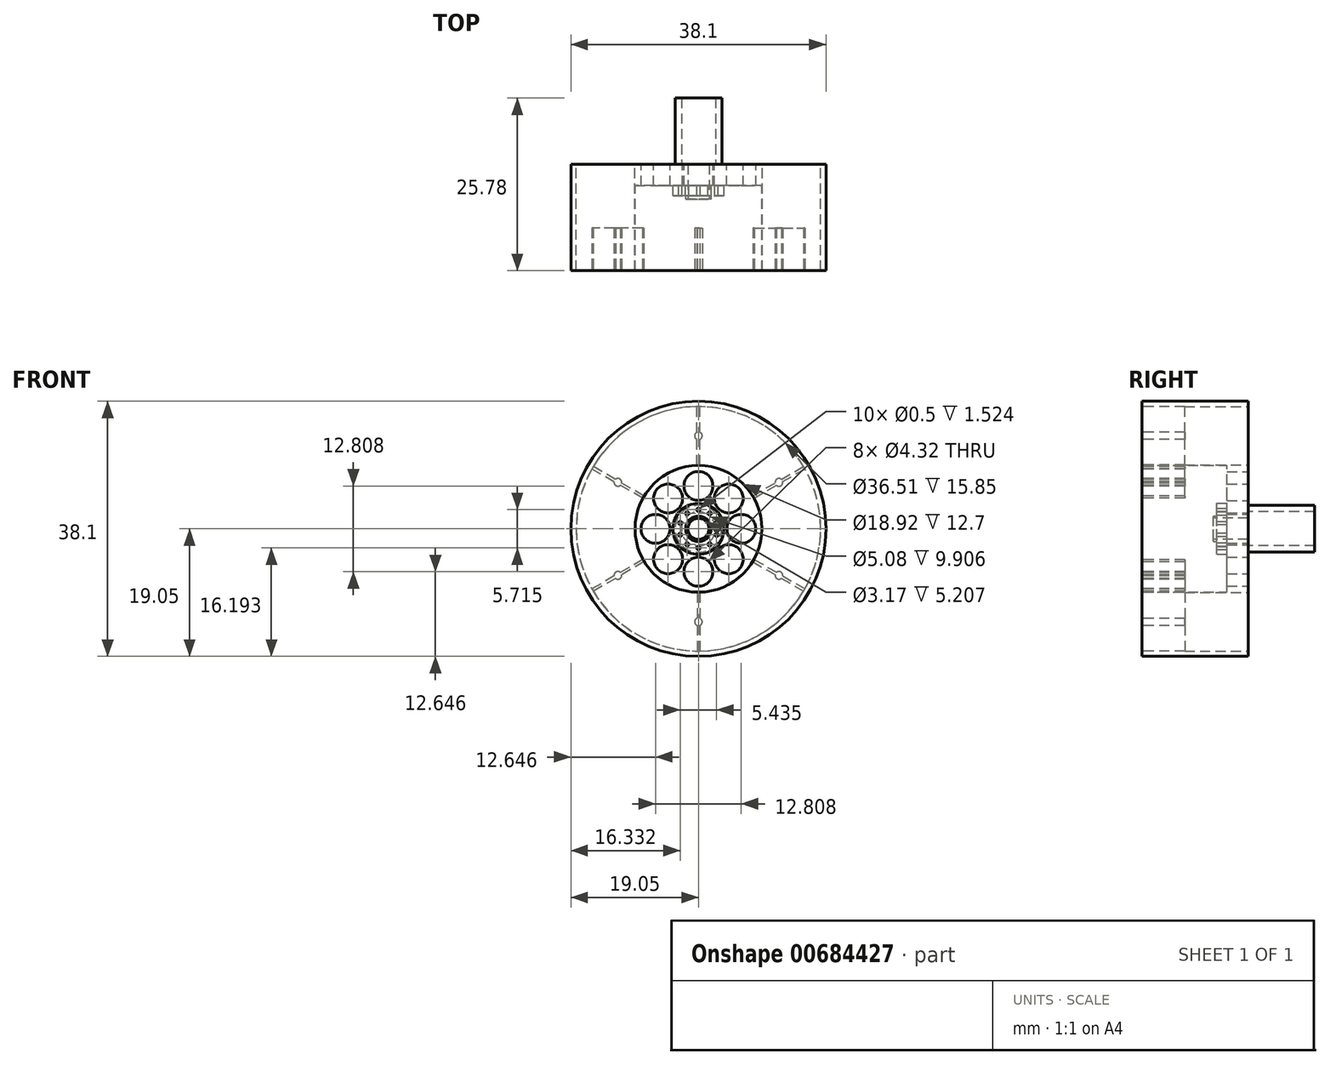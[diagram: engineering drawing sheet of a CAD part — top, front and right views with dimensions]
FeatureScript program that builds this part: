
annotation { "Feature Type Name" : "Feature", "Feature Type Description" : "" }
export const myFeature = defineFeature(function(context is Context, id is Id, definition is map)
    precondition{}
    {
        {
            var Q0;
            Q0=qCreatedBy(makeId("Front.planeOp"),FACE);
            var sketch = newSketch(context, id + "F0", { "sketchPlane" : qUnion([Q0])});
            skCircle(sketch, "E0", {"center": v(0, 0) * mm, "radius": 19.05 * mm});
            skCircle(sketch, "E1", {"center": v(0, 0) * mm, "radius": 17.46 * mm});
            skSolve(sketch);
        }
        {
            var Q0;
            Q0 = qSketchRegion(id + "F0", true);
            extrude(context, id + "F1", {"entities" : qUnion([Q0]), "oppositeDirection" : true, "depth" : 15.88 * mm, "offsetDistance" : 25.4 * mm});
        }
        {
            var Q0;
            Q0=makeQuery(id+"F0.imprint","IMPRINT",FACE,{"disambiguationData":[TD([[makeQuery(id+"F0.imprint","IMPRINT",EDGE,{"derivedFrom":sQuery(id+"F0.wireOp",EDGE,"E1")}),1.0]])]});
            extrude(context, id + "F2", {"entities" : qUnion([Q0]), "operationType" : NewBodyOperationType.ADD, "oppositeDirection" : true, "depth" : 15.88 * mm, "offsetDistance" : 25.4 * mm});
        }
        {
            var Q0;
            {var subQ0=sQuery(id+"F0.wireOp",EDGE,"E1");Q0=makeQuery(id+"F2.boolean.opBoolean","MERGE",FACE,{"derivedFrom":[makeQuery(id+"F1.opExtrude","CAP_FACE",FACE,{"disambiguationData":[OSD([sQuery(id+"F0.wireOp",EDGE,"E0"),subQ0])],"isStart":true}),makeQuery(id+"F2.opExtrude","CAP_FACE",FACE,{"disambiguationData":[OSD([subQ0])],"isStart":true})]});}
            var sketch = newSketch(context, id + "F3", { "sketchPlane" : qUnion([Q0])});
            skCircle(sketch, "E2", {"center": v(0, 0) * mm, "radius": 9.53 * mm});
            skSolve(sketch);
        }
        {
            var Q0;
            Q0=makeQuery(id+"F3.imprint","IMPRINT",FACE,{"disambiguationData":[TD([[makeQuery(id+"F3.imprint","IMPRINT",EDGE,{"derivedFrom":sQuery(id+"F3.wireOp",EDGE,"E2")}),1.0]])]});
            extrude(context, id + "F4", {"entities" : qUnion([Q0]), "operationType" : NewBodyOperationType.REMOVE, "oppositeDirection" : true, "depth" : 12.7 * mm, "offsetDistance" : 25.4 * mm});
        }
        {
            var Q0;
            {var subQ0=sQuery(id+"F0.wireOp",EDGE,"E1");Q0=makeQuery(id+"F2.boolean.opBoolean","MERGE",FACE,{"derivedFrom":[makeQuery(id+"F1.opExtrude","CAP_FACE",FACE,{"disambiguationData":[OSD([sQuery(id+"F0.wireOp",EDGE,"E0"),subQ0])],"isStart":false}),makeQuery(id+"F2.opExtrude","CAP_FACE",FACE,{"disambiguationData":[OSD([subQ0])],"isStart":false})]});}
            var sketch = newSketch(context, id + "F5", { "sketchPlane" : qUnion([Q0])});
            skCircle(sketch, "E3", {"center": v(0, 0) * mm, "radius": 18.26 * mm});
            skCircle(sketch, "E4", {"center": v(0, 0) * mm, "radius": 9.53 * mm});
            skSolve(sketch);
        }
        {
            var Q0;
            Q0=makeQuery(id+"F5.imprint","IMPRINT",FACE,{"disambiguationData":[TD([[makeQuery(id+"F5.imprint","IMPRINT",EDGE,{"derivedFrom":sQuery(id+"F5.wireOp",EDGE,"E3")}),1.0]])]});
            extrude(context, id + "F6", {"entities" : qUnion([Q0]), "operationType" : NewBodyOperationType.REMOVE, "oppositeDirection" : true, "depth" : 15.85 * mm, "offsetDistance" : 25.4 * mm});
        }
        {
            var Q0;
            Q0=makeQuery(id+"F4.boolean.opBoolean","COPY",FACE,{"derivedFrom":makeQuery(id+"F4.opExtrude","CAP_FACE",FACE,{"disambiguationData":[OSD([sQuery(id+"F3.wireOp",EDGE,"E2")])],"isStart":false})});
            var sketch = newSketch(context, id + "F7", { "sketchPlane" : qUnion([Q0])});
            skCircle(sketch, "E5", {"center": v(0, 0) * mm, "radius": 9.52 * mm});
            skCircle(sketch, "E6", {"center": v(0, 0) * mm, "radius": 9.46 * mm});
            skSolve(sketch);
        }
        {
            var Q0;
            Q0=makeQuery(id+"F7.imprint","IMPRINT",FACE,{"disambiguationData":[TD([[makeQuery(id+"F7.imprint","IMPRINT",EDGE,{"derivedFrom":sQuery(id+"F7.wireOp",EDGE,"E5")}),1.0]])]});
            var Q1;
            Q1=sQuery(id+"F7.wireOp",EDGE,"E5");
            extrude(context, id + "F8", {"entities" : qUnion([Q0]), "operationType" : NewBodyOperationType.ADD, "surfaceEntities" : qUnion([Q1]), "depth" : 12.7 * mm, "offsetDistance" : 25.4 * mm, "surfaceOperationType" : NewSurfaceOperationType.ADD});
        }
        {
            var Q0;
            {var subQ0=sQuery(id+"F0.wireOp",EDGE,"E1");Q0=makeQuery(id+"F6.boolean.opBoolean","SPLIT",FACE,{"disambiguationData":[TD([makeQuery(id+"F6.opExtrude","SWEPT_FACE",FACE,{"disambiguationData":[OSD([sQuery(id+"F5.wireOp",EDGE,"E4")])]})])],"derivedFrom":makeQuery(id+"F2.boolean.opBoolean","MERGE",FACE,{"derivedFrom":[makeQuery(id+"F1.opExtrude","CAP_FACE",FACE,{"disambiguationData":[OSD([sQuery(id+"F0.wireOp",EDGE,"E0"),subQ0])],"isStart":false}),makeQuery(id+"F2.opExtrude","CAP_FACE",FACE,{"disambiguationData":[OSD([subQ0])],"isStart":false})]})});}
            var sketch = newSketch(context, id + "F9", { "sketchPlane" : qUnion([Q0])});
            skLineSegment(sketch, "E7", {"start": v(0, 6) * mm, "end": v(0, 6.2) * mm});
            skLineSegment(sketch, "E8", {"start": v(0, 6.2) * mm, "end": v(0, 6.4) * mm});
            skCircle(sketch, "E9", {"center": v(0, 6.4) * mm, "radius": 2.16 * mm});
            skCircle(sketch, "E10.1.0", {"center": v(-4.53, 4.53) * mm, "radius": 2.16 * mm});
            skCircle(sketch, "E10.2.0", {"center": v(-6.4, 0) * mm, "radius": 2.16 * mm});
            skCircle(sketch, "E10.3.0", {"center": v(-4.53, -4.53) * mm, "radius": 2.16 * mm});
            skCircle(sketch, "E10.4.0", {"center": v(0, -6.4) * mm, "radius": 2.16 * mm});
            skCircle(sketch, "E10.5.0", {"center": v(4.53, -4.53) * mm, "radius": 2.16 * mm});
            skCircle(sketch, "E10.6.0", {"center": v(6.4, 0) * mm, "radius": 2.16 * mm});
            skCircle(sketch, "E10.7.0", {"center": v(4.53, 4.53) * mm, "radius": 2.16 * mm});
            skPoint(sketch, "E10.center", {"position": v(0, 0) * mm});
            skSolve(sketch);
        }
        {
            var Q0;
            Q0=makeQuery(id+"F9.imprint","IMPRINT",FACE,{"disambiguationData":[TD([[makeQuery(id+"F9.imprint","IMPRINT",EDGE,{"derivedFrom":sQuery(id+"F9.wireOp",EDGE,"E10.1.0")}),1.0]])]});
            var Q1;
            Q1=makeQuery(id+"F9.imprint","IMPRINT",FACE,{"disambiguationData":[TD([[makeQuery(id+"F9.imprint","IMPRINT",EDGE,{"derivedFrom":sQuery(id+"F9.wireOp",EDGE,"E10.2.0")}),1.0]])]});
            var Q2;
            Q2=makeQuery(id+"F9.imprint","IMPRINT",FACE,{"disambiguationData":[TD([[makeQuery(id+"F9.imprint","IMPRINT",EDGE,{"derivedFrom":sQuery(id+"F9.wireOp",EDGE,"E10.3.0")}),1.0]])]});
            var Q3;
            Q3=makeQuery(id+"F9.imprint","IMPRINT",FACE,{"disambiguationData":[TD([[makeQuery(id+"F9.imprint","IMPRINT",EDGE,{"derivedFrom":sQuery(id+"F9.wireOp",EDGE,"E10.4.0")}),1.0]])]});
            var Q4;
            Q4=makeQuery(id+"F9.imprint","IMPRINT",FACE,{"disambiguationData":[TD([[makeQuery(id+"F9.imprint","IMPRINT",EDGE,{"derivedFrom":sQuery(id+"F9.wireOp",EDGE,"E10.5.0")}),1.0]])]});
            var Q5;
            Q5=makeQuery(id+"F9.imprint","IMPRINT",FACE,{"disambiguationData":[TD([[makeQuery(id+"F9.imprint","IMPRINT",EDGE,{"derivedFrom":sQuery(id+"F9.wireOp",EDGE,"E10.6.0")}),1.0]])]});
            var Q6;
            Q6=makeQuery(id+"F9.imprint","IMPRINT",FACE,{"disambiguationData":[TD([[makeQuery(id+"F9.imprint","IMPRINT",EDGE,{"derivedFrom":sQuery(id+"F9.wireOp",EDGE,"E10.7.0")}),1.0]])]});
            var Q7;
            Q7=makeQuery(id+"F9.imprint","IMPRINT",FACE,{"disambiguationData":[TD([[makeQuery(id+"F9.imprint","IMPRINT",EDGE,{"derivedFrom":sQuery(id+"F9.wireOp",EDGE,"E9")}),1.0]])]});
            extrude(context, id + "F10", {"entities" : qUnion([Q0, Q1, Q2, Q3, Q4, Q5, Q6, Q7]), "operationType" : NewBodyOperationType.REMOVE, "oppositeDirection" : true, "depth" : 25.4 * mm, "offsetDistance" : 25.4 * mm});
        }
        {
            var Q0;
            Q0=makeQuery(id+"F4.boolean.opBoolean","COPY",FACE,{"derivedFrom":makeQuery(id+"F4.opExtrude","CAP_FACE",FACE,{"disambiguationData":[OSD([sQuery(id+"F3.wireOp",EDGE,"E2")])],"isStart":false})});
            var sketch = newSketch(context, id + "F11", { "sketchPlane" : qUnion([Q0])});
            skCircle(sketch, "E11", {"center": v(0, 0) * mm, "radius": 3.8 * mm});
            skCircle(sketch, "E12", {"center": v(0, 0) * mm, "radius": 1.9 * mm});
            skLineSegment(sketch, "E13", {"start": v(0, 1.9) * mm, "end": v(0, 2.86) * mm});
            skCircle(sketch, "E14", {"center": v(0, 2.86) * mm, "radius": 0.25 * mm});
            skCircle(sketch, "E15.1.0", {"center": v(-1.68, 2.31) * mm, "radius": 0.25 * mm});
            skCircle(sketch, "E15.2.0", {"center": v(-2.72, 0.88) * mm, "radius": 0.25 * mm});
            skCircle(sketch, "E15.3.0", {"center": v(-2.72, -0.88) * mm, "radius": 0.25 * mm});
            skCircle(sketch, "E15.4.0", {"center": v(-1.68, -2.31) * mm, "radius": 0.25 * mm});
            skCircle(sketch, "E15.5.0", {"center": v(0, -2.86) * mm, "radius": 0.25 * mm});
            skCircle(sketch, "E15.6.0", {"center": v(1.68, -2.31) * mm, "radius": 0.25 * mm});
            skCircle(sketch, "E15.7.0", {"center": v(2.72, -0.88) * mm, "radius": 0.25 * mm});
            skCircle(sketch, "E15.8.0", {"center": v(2.72, 0.88) * mm, "radius": 0.25 * mm});
            skCircle(sketch, "E15.9.0", {"center": v(1.68, 2.31) * mm, "radius": 0.25 * mm});
            skSolve(sketch);
        }
        {
            var Q0;
            Q0=makeQuery(id+"F11.imprint","IMPRINT",FACE,{"disambiguationData":[TD([[makeQuery(id+"F11.imprint","IMPRINT",EDGE,{"derivedFrom":sQuery(id+"F11.wireOp",EDGE,"E11")}),1.0]])]});
            extrude(context, id + "F12", {"entities" : qUnion([Q0]), "operationType" : NewBodyOperationType.ADD, "depth" : 1.52 * mm, "offsetDistance" : 25.4 * mm});
        }
        {
            var Q0;
            Q0=makeQuery(id+"F12.boolean.opBoolean","SPLIT",FACE,{"disambiguationData":[TD([makeQuery(id+"F12.opExtrude","SWEPT_FACE",FACE,{"disambiguationData":[OSD([sQuery(id+"F11.wireOp",EDGE,"E12")])]})])],"derivedFrom":makeQuery(id+"F4.boolean.opBoolean","COPY",FACE,{"derivedFrom":makeQuery(id+"F4.opExtrude","CAP_FACE",FACE,{"disambiguationData":[OSD([sQuery(id+"F3.wireOp",EDGE,"E2")])],"isStart":false})})});
            extrude(context, id + "F13", {"entities" : qUnion([Q0]), "operationType" : NewBodyOperationType.ADD, "depth" : 2.03 * mm, "offsetDistance" : 25.4 * mm});
        }
        {
            var Q0;
            {var subQ0=sQuery(id+"F0.wireOp",EDGE,"E1");Q0=makeQuery(id+"F6.boolean.opBoolean","SPLIT",FACE,{"disambiguationData":[TD([makeQuery(id+"F6.opExtrude","SWEPT_FACE",FACE,{"disambiguationData":[OSD([sQuery(id+"F5.wireOp",EDGE,"E4")])]})])],"derivedFrom":makeQuery(id+"F2.boolean.opBoolean","MERGE",FACE,{"derivedFrom":[makeQuery(id+"F1.opExtrude","CAP_FACE",FACE,{"disambiguationData":[OSD([sQuery(id+"F0.wireOp",EDGE,"E0"),subQ0])],"isStart":false}),makeQuery(id+"F2.opExtrude","CAP_FACE",FACE,{"disambiguationData":[OSD([subQ0])],"isStart":false})]})});}
            var sketch = newSketch(context, id + "F14", { "sketchPlane" : qUnion([Q0])});
            skCircle(sketch, "E16", {"center": v(0, 0) * mm, "radius": 3.5 * mm});
            skCircle(sketch, "E17", {"center": v(0, 0) * mm, "radius": 2.54 * mm});
            skSolve(sketch);
        }
        {
            var Q0;
            Q0=makeQuery(id+"F14.imprint","IMPRINT",FACE,{"disambiguationData":[TD([[makeQuery(id+"F14.imprint","IMPRINT",EDGE,{"derivedFrom":sQuery(id+"F14.wireOp",EDGE,"E16")}),1.0]])]});
            extrude(context, id + "F15", {"entities" : qUnion([Q0]), "operationType" : NewBodyOperationType.ADD, "depth" : 9.9 * mm, "offsetDistance" : 25.4 * mm});
        }
        {
            var Q0;
            Q0=makeQuery(id+"F6.boolean.opBoolean","COPY",FACE,{"derivedFrom":makeQuery(id+"F6.opExtrude","CAP_FACE",FACE,{"disambiguationData":[OSD([sQuery(id+"F5.wireOp",EDGE,"E3"),sQuery(id+"F5.wireOp",EDGE,"E4")])],"isStart":false})});
            var sketch = newSketch(context, id + "F16", { "sketchPlane" : qUnion([Q0])});
            skLineSegment(sketch, "E18", {"start": v(0, 9.53) * mm, "end": v(0.21, 9.52) * mm});
            skLineSegment(sketch, "E19", {"start": v(0, 9.53) * mm, "end": v(-0.2, 9.52) * mm});
            skLineSegment(sketch, "E20", {"start": v(-0.2, 9.52) * mm, "end": v(-0.2, 13.35) * mm});
            skLineSegment(sketch, "E21", {"start": v(0.21, 9.52) * mm, "end": v(0.21, 13.36) * mm});
            skPoint(sketch, "E22.endSnap0", {"position": v(0.21, 13.89) * mm});
            skArc(sketch, "E23", {"start": v(-0.2, 14.43) * mm, "mid": v(-0.57, 13.89) * mm, "end": v(-0.2, 13.35) * mm});
            skArc(sketch, "E24.trimOffspring", {"start": v(0.21, 13.36) * mm, "mid": v(0.57, 13.89) * mm, "end": v(0.21, 14.42) * mm});
            skLineSegment(sketch, "E25.trimOffspring", {"start": v(-0.2, 14.43) * mm, "end": v(-0.2, 18.26) * mm});
            skLineSegment(sketch, "E26.trimOffspring", {"start": v(0.21, 14.42) * mm, "end": v(0.21, 18.26) * mm});
            skLineSegment(sketch, "E27.1.0", {"start": v(-12.6, 7.05) * mm, "end": v(-15.9, 8.96) * mm});
            skLineSegment(sketch, "E27.1.1", {"start": v(-12.38, 7.4) * mm, "end": v(-15.7, 9.3) * mm});
            skArc(sketch, "E27.1.2", {"start": v(-12.6, 7.05) * mm, "mid": v(-12.31, 6.45) * mm, "end": v(-11.66, 6.5) * mm});
            skArc(sketch, "E27.1.3", {"start": v(-11.46, 6.86) * mm, "mid": v(-11.74, 7.44) * mm, "end": v(-12.38, 7.4) * mm});
            skLineSegment(sketch, "E27.1.4", {"start": v(-8.14, 4.94) * mm, "end": v(-11.46, 6.86) * mm});
            skLineSegment(sketch, "E27.1.5", {"start": v(-8.34, 4.6) * mm, "end": v(-11.66, 6.5) * mm});
            skLineSegment(sketch, "E27.2.0", {"start": v(-12.4, -7.38) * mm, "end": v(-15.71, -9.3) * mm});
            skLineSegment(sketch, "E27.2.1", {"start": v(-12.6, -7.03) * mm, "end": v(-15.91, -8.95) * mm});
            skArc(sketch, "E27.2.2", {"start": v(-12.4, -7.38) * mm, "mid": v(-11.74, -7.44) * mm, "end": v(-11.47, -6.84) * mm});
            skArc(sketch, "E27.2.3", {"start": v(-11.67, -6.5) * mm, "mid": v(-12.31, -6.45) * mm, "end": v(-12.6, -7.03) * mm});
            skLineSegment(sketch, "E27.2.4", {"start": v(-8.35, -4.58) * mm, "end": v(-11.67, -6.5) * mm});
            skLineSegment(sketch, "E27.2.5", {"start": v(-8.15, -4.93) * mm, "end": v(-11.47, -6.84) * mm});
            skLineSegment(sketch, "E27.3.0", {"start": v(0.2, -14.43) * mm, "end": v(0.2, -18.26) * mm});
            skLineSegment(sketch, "E27.3.1", {"start": v(-0.21, -14.42) * mm, "end": v(-0.21, -18.26) * mm});
            skArc(sketch, "E27.3.2", {"start": v(0.2, -14.43) * mm, "mid": v(0.57, -13.89) * mm, "end": v(0.2, -13.35) * mm});
            skArc(sketch, "E27.3.3", {"start": v(-0.21, -13.36) * mm, "mid": v(-0.57, -13.89) * mm, "end": v(-0.21, -14.42) * mm});
            skLineSegment(sketch, "E27.3.4", {"start": v(-0.21, -9.52) * mm, "end": v(-0.21, -13.36) * mm});
            skLineSegment(sketch, "E27.3.5", {"start": v(0.2, -9.52) * mm, "end": v(0.2, -13.35) * mm});
            skLineSegment(sketch, "E27.4.0", {"start": v(12.6, -7.05) * mm, "end": v(15.9, -8.96) * mm});
            skLineSegment(sketch, "E27.4.1", {"start": v(12.38, -7.4) * mm, "end": v(15.7, -9.3) * mm});
            skArc(sketch, "E27.4.2", {"start": v(12.6, -7.05) * mm, "mid": v(12.31, -6.45) * mm, "end": v(11.66, -6.5) * mm});
            skArc(sketch, "E27.4.3", {"start": v(11.46, -6.86) * mm, "mid": v(11.74, -7.44) * mm, "end": v(12.38, -7.4) * mm});
            skLineSegment(sketch, "E27.4.4", {"start": v(8.14, -4.94) * mm, "end": v(11.46, -6.86) * mm});
            skLineSegment(sketch, "E27.4.5", {"start": v(8.34, -4.6) * mm, "end": v(11.66, -6.5) * mm});
            skLineSegment(sketch, "E27.5.0", {"start": v(12.4, 7.38) * mm, "end": v(15.71, 9.3) * mm});
            skLineSegment(sketch, "E27.5.1", {"start": v(12.6, 7.03) * mm, "end": v(15.91, 8.95) * mm});
            skArc(sketch, "E27.5.2", {"start": v(12.4, 7.38) * mm, "mid": v(11.74, 7.44) * mm, "end": v(11.47, 6.84) * mm});
            skArc(sketch, "E27.5.3", {"start": v(11.67, 6.5) * mm, "mid": v(12.31, 6.45) * mm, "end": v(12.6, 7.03) * mm});
            skLineSegment(sketch, "E27.5.4", {"start": v(8.35, 4.58) * mm, "end": v(11.67, 6.5) * mm});
            skLineSegment(sketch, "E27.5.5", {"start": v(8.15, 4.93) * mm, "end": v(11.47, 6.84) * mm});
            skPoint(sketch, "E27.center", {"position": v(0, 0) * mm});
            skSolve(sketch);
        }
        {
            var Q0;
            {var subQ4=sQuery(id+"F16.wireOp",EDGE,"E20");Q0=makeQuery(id+"F16.imprint","IMPRINT",FACE,{"disambiguationData":[TD([[makeQuery(id+"F16.imprint","IMPRINT",EDGE,{"derivedFrom":subQ4}),-1.0]])]});}
            var Q1;
            {var subQ4=sQuery(id+"F16.wireOp",EDGE,"E27.1.0");Q1=makeQuery(id+"F16.imprint","IMPRINT",FACE,{"disambiguationData":[TD([[makeQuery(id+"F16.imprint","IMPRINT",EDGE,{"derivedFrom":subQ4}),-1.0]])]});}
            var Q2;
            {var subQ1=sQuery(id+"F16.wireOp",EDGE,"E27.2.0");Q2=makeQuery(id+"F16.imprint","IMPRINT",FACE,{"disambiguationData":[TD([[makeQuery(id+"F16.imprint","IMPRINT",EDGE,{"derivedFrom":subQ1}),-1.0]])]});}
            var Q3;
            {var subQ0=sQuery(id+"F16.wireOp",EDGE,"E27.3.0");Q3=makeQuery(id+"F16.imprint","IMPRINT",FACE,{"disambiguationData":[TD([[makeQuery(id+"F16.imprint","IMPRINT",EDGE,{"derivedFrom":subQ0}),-1.0]])]});}
            var Q4;
            {var subQ4=sQuery(id+"F16.wireOp",EDGE,"E27.4.0");Q4=makeQuery(id+"F16.imprint","IMPRINT",FACE,{"disambiguationData":[TD([[makeQuery(id+"F16.imprint","IMPRINT",EDGE,{"derivedFrom":subQ4}),-1.0]])]});}
            var Q5;
            {var subQ1=sQuery(id+"F16.wireOp",EDGE,"E27.5.0");Q5=makeQuery(id+"F16.imprint","IMPRINT",FACE,{"disambiguationData":[TD([[makeQuery(id+"F16.imprint","IMPRINT",EDGE,{"derivedFrom":subQ1}),-1.0]])]});}
            extrude(context, id + "F17", {"entities" : qUnion([Q0, Q1, Q2, Q3, Q4, Q5]), "operationType" : NewBodyOperationType.ADD, "depth" : 6.35 * mm, "offsetDistance" : 25.4 * mm});
        }
        {
            var Q0;
            Q0=makeQuery(id+"F13.opExtrude","CAP_FACE",FACE,{"disambiguationData":[OSD([sQuery(id+"F3.wireOp",EDGE,"E2")])],"isStart":false});
            var sketch = newSketch(context, id + "F18", { "sketchPlane" : qUnion([Q0])});
            skCircle(sketch, "E28", {"center": v(0, 0) * mm, "radius": 1.59 * mm});
            skSolve(sketch);
        }
        {
            var Q0;
            Q0=makeQuery(id+"F18.imprint","IMPRINT",FACE,{"disambiguationData":[TD([[makeQuery(id+"F18.imprint","IMPRINT",EDGE,{"derivedFrom":sQuery(id+"F18.wireOp",EDGE,"E28")}),1.0]])]});
            extrude(context, id + "F19", {"entities" : qUnion([Q0]), "operationType" : NewBodyOperationType.REMOVE, "oppositeDirection" : true, "depth" : 25.4 * mm, "offsetDistance" : 25.4 * mm});
        }
    });
